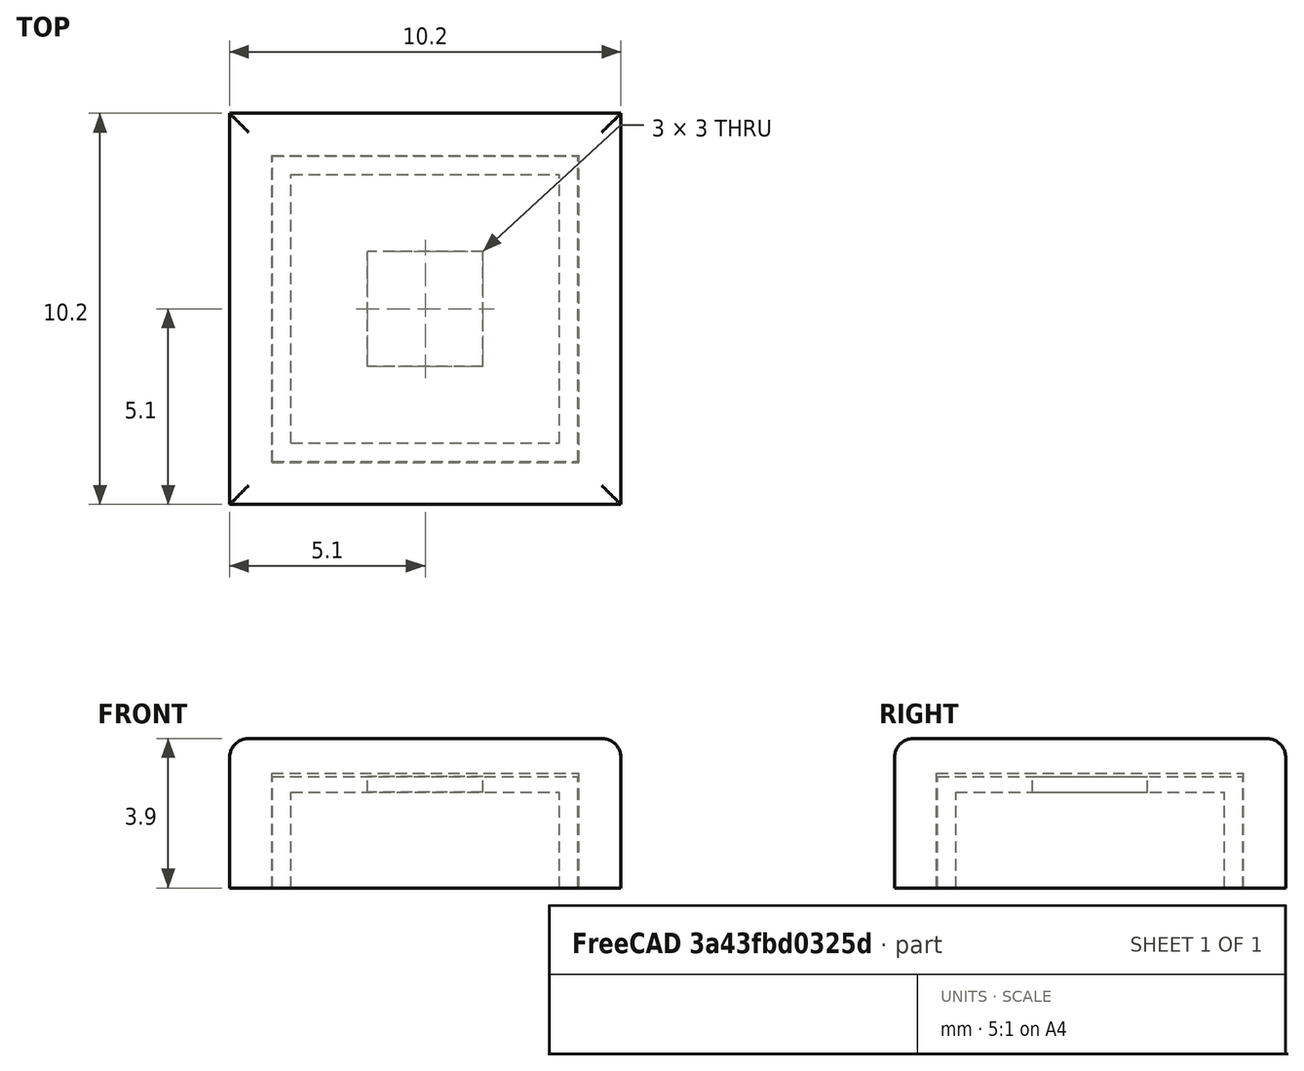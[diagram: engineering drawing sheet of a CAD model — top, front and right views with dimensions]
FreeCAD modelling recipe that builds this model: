
FCSTD DOCUMENT  (FreeCAD 0.17R13541 (Git))
Label: E-Switch_TL3240S1CAPIVR
License: All rights reserved
LicenseURL: http://en.wikipedia.org/wiki/All_rights_reserved
objects: Part::Box×5, Part::Cut×2, Part::Fillet×1, Part::Fuse×1, App::Part×1
note: 9 computed .brp shape members not serialized (recipe doc carries the construction recipe); baked Part::Feature solids carry a one-line shape summary decoded from their .brp

FEATURE [Part::Box] Box  label="Cube"
  AttacherType = Attacher::AttachEngine3D
  Height = 3.9
  Length = 10.2
  Placement = pos=(-5.1,-5.1,0) rot=(0,0,1;0rad)
  Width = 10.2
FEATURE [Part::Box] Box001  label="Cube001"
  AttacherType = Attacher::AttachEngine3D
  Height = 3
  Length = 8
  Placement = pos=(-4,-4,0) rot=(0,0,1;0rad)
  Width = 8
FEATURE [Part::Cut] Cut
  Base = -> Box
  Tool = -> Box001
FEATURE [Part::Fillet] Fillet
  Base = -> Cut
  Edges = 4 edges r=0.5: [Edge2,Edge7,Edge8,Edge9]
FEATURE [Part::Box] Box002  label="Cube002"
  AttacherType = Attacher::AttachEngine3D
  Height = 2.9
  Length = 7.96
  Placement = pos=(-3.98,-3.98,0) rot=(0,0,1;0rad)
  Width = 7.96
FEATURE [Part::Box] Box003  label="Cube003"
  AttacherType = Attacher::AttachEngine3D
  Height = 2.5
  Length = 7
  Placement = pos=(-3.5,-3.5,0) rot=(0,0,1;0rad)
  Width = 7
FEATURE [Part::Box] Box004  label="Cube004"
  AttacherType = Attacher::AttachEngine3D
  Height = 4
  Length = 3
  Placement = pos=(-1.5,-1.5,0) rot=(0,0,1;0rad)
  Width = 3
FEATURE [Part::Fuse] Fusion
  Base = -> Box003
  Tool = -> Box004
FEATURE [Part::Cut] Cut001
  Base = -> Box002
  Tool = -> Fusion
FEATURE [App::Part] Part
  Group = -> [Cut,Box001,Box,Fillet,Fusion,Box003,Box004,Box002,Cut001]
  License = CC BY 3.0
  LicenseURL = http://creativecommons.org/licenses/by/3.0/
  Origin = -> Origin
